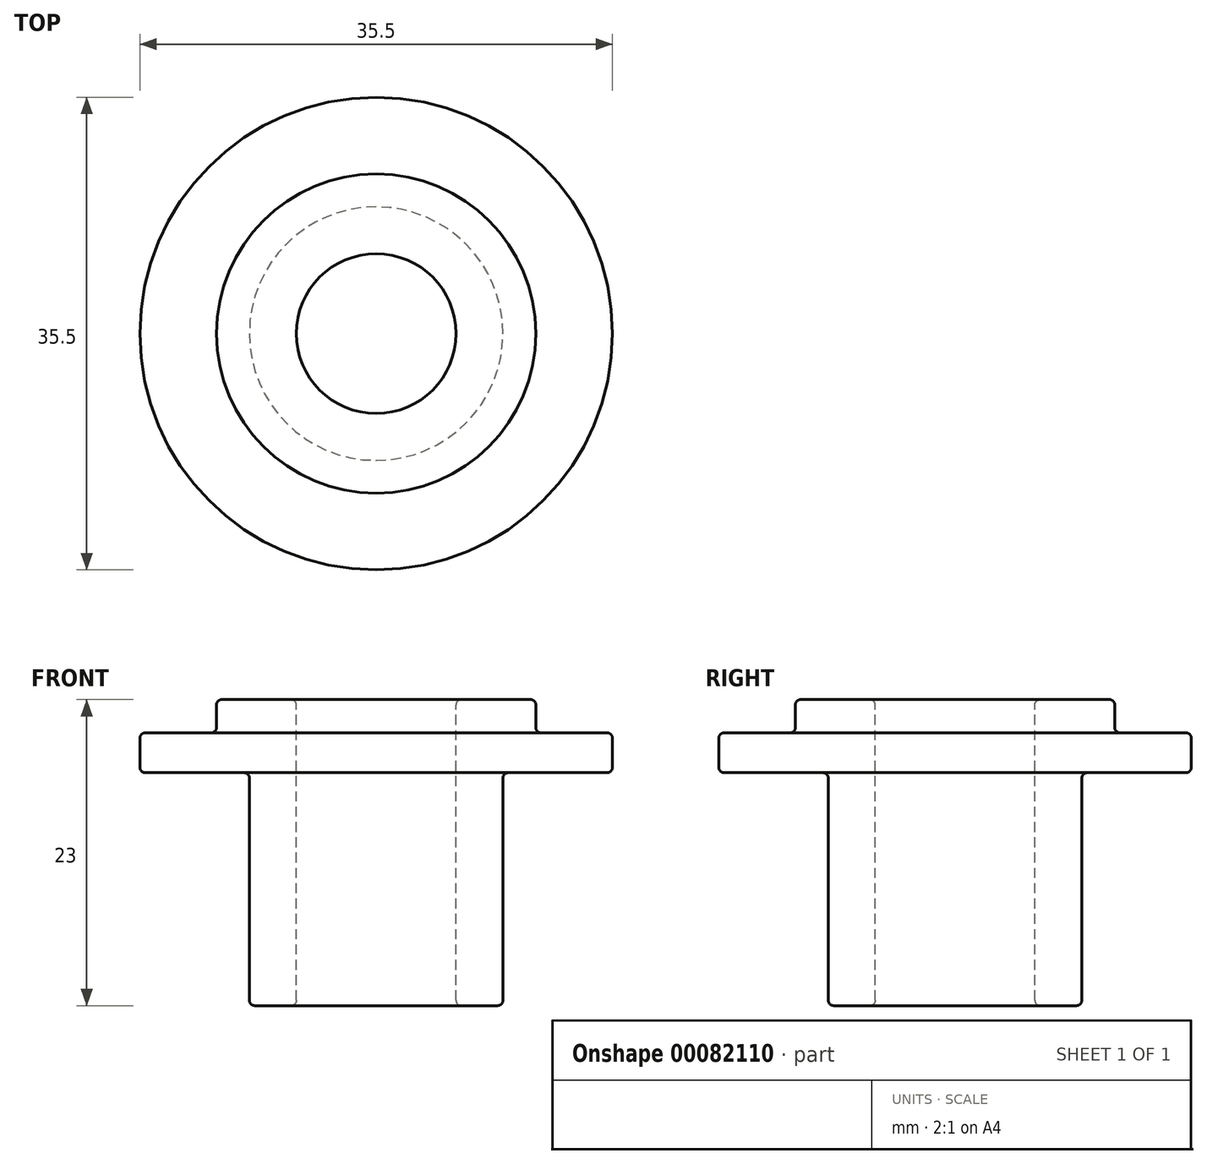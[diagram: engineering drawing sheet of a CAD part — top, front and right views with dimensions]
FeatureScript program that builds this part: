
annotation { "Feature Type Name" : "Feature", "Feature Type Description" : "" }
export const myFeature = defineFeature(function(context is Context, id is Id, definition is map)
    precondition{}
    {
        {
            var Q0;
            Q0=qCreatedBy(makeId("Top.planeOp"),FACE);
            var sketch = newSketch(context, id + "F0", { "sketchPlane" : qUnion([Q0])});
            skCircle(sketch, "E0", {"center": v(0, 0) * mm, "radius": 9.53 * mm});
            skCircle(sketch, "E1", {"center": v(0, 0) * mm, "radius": 6 * mm});
            skSolve(sketch);
        }
        {
            var Q0;
            Q0 = qSketchRegion(id + "F0", true);
            extrude(context, id + "F1", {"entities" : qUnion([Q0]), "oppositeDirection" : true, "depth" : 17.5 * mm});
        }
        {
            var Q0;
            Q0=qCreatedBy(makeId("Top.planeOp"),FACE);
            var sketch = newSketch(context, id + "F2", { "sketchPlane" : qUnion([Q0])});
            skCircle(sketch, "E2", {"center": v(0, 0) * mm, "radius": 17.75 * mm});
            skCircle(sketch, "E3.0", {"center": v(0, 0) * mm, "radius": 6 * mm});
            skSolve(sketch);
        }
        {
            var Q0;
            Q0 = qSketchRegion(id + "F2", true);
            extrude(context, id + "F3", {"entities" : qUnion([Q0]), "operationType" : NewBodyOperationType.ADD, "depth" : 3 * mm});
        }
        {
            var Q0;
            Q0=makeQuery(id+"F3.opExtrude","CAP_FACE",FACE,{"disambiguationData":[OSD([sQuery(id+"F2.wireOp",EDGE,"E2"),sQuery(id+"F2.wireOp",EDGE,"E3.0")])],"isStart":false});
            var sketch = newSketch(context, id + "F4", { "sketchPlane" : qUnion([Q0])});
            skCircle(sketch, "E4.0", {"center": v(0, 0) * mm, "radius": 6 * mm});
            skCircle(sketch, "E5", {"center": v(0, 0) * mm, "radius": 12 * mm});
            skSolve(sketch);
        }
        {
            var Q0;
            Q0 = qSketchRegion(id + "F4", true);
            extrude(context, id + "F5", {"entities" : qUnion([Q0]), "operationType" : NewBodyOperationType.ADD, "depth" : 2.5 * mm});
        }
        {
            var Q0;
            Q0=makeQuery(id+"F5.opExtrude","CAP_FACE",FACE,{"disambiguationData":[OSD([sQuery(id+"F4.wireOp",EDGE,"E4.0"),sQuery(id+"F4.wireOp",EDGE,"E5")])],"isStart":false});
            var Q1;
            Q1=makeQuery(id+"F3.opExtrude","CAP_FACE",FACE,{"disambiguationData":[OSD([sQuery(id+"F2.wireOp",EDGE,"E2"),sQuery(id+"F2.wireOp",EDGE,"E3.0")])],"isStart":false});
            var Q2;
            Q2=makeQuery(id+"F3.opExtrude","CAP_FACE",FACE,{"disambiguationData":[OSD([sQuery(id+"F2.wireOp",EDGE,"E2"),sQuery(id+"F2.wireOp",EDGE,"E3.0")])],"isStart":true});
            var Q3;
            Q3=makeQuery(id+"F1.opExtrude","CAP_FACE",FACE,{"disambiguationData":[OSD([sQuery(id+"F0.wireOp",EDGE,"E0"),sQuery(id+"F0.wireOp",EDGE,"E1")])],"isStart":false});
            fillet(context, id + "F6", {"entities" : qUnion([Q0, Q1, Q2, Q3]), "radius" : 0.4 * mm, "tangentPropagation" : true, "allowEdgeOverflow" : false});
        }
    });
